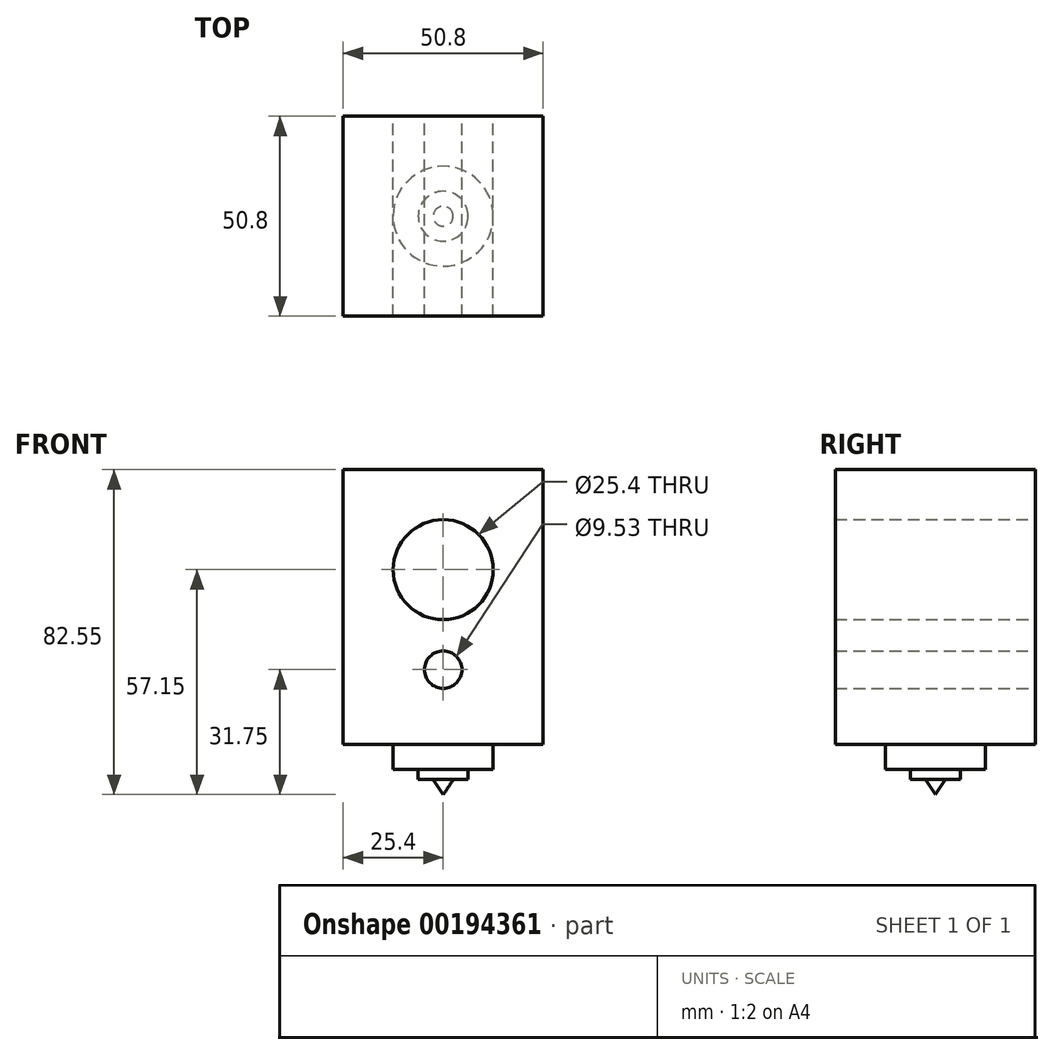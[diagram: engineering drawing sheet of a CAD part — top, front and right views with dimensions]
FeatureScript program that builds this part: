
annotation { "Feature Type Name" : "Feature", "Feature Type Description" : "" }
export const myFeature = defineFeature(function(context is Context, id is Id, definition is map)
    precondition{}
    {
        {
            var Q0;
            Q0=qCreatedBy(makeId("Front.planeOp"),FACE);
            var sketch = newSketch(context, id + "F0", { "sketchPlane" : qUnion([Q0])});
            skCircle(sketch, "E0", {"center": v(0, 0) * mm, "radius": 12.7 * mm});
            skCircle(sketch, "E1", {"center": v(0, -25.4) * mm, "radius": 4.76 * mm});
            skLineSegment(sketch, "E2.bottom", {"start": v(-25.4, -44.45) * mm, "end": v(25.4, -44.45) * mm});
            skLineSegment(sketch, "E2.top", {"start": v(-25.4, 25.4) * mm, "end": v(25.4, 25.4) * mm});
            skLineSegment(sketch, "E2.left", {"start": v(-25.4, -44.45) * mm, "end": v(-25.4, 25.4) * mm});
            skLineSegment(sketch, "E2.right", {"start": v(25.4, -44.45) * mm, "end": v(25.4, 25.4) * mm});
            skLineSegment(sketch, "E3", {"start": v(-12.7, -44.45) * mm, "end": v(-12.7, -50.8) * mm});
            skLineSegment(sketch, "E4", {"start": v(-12.7, -50.8) * mm, "end": v(12.7, -50.8) * mm});
            skLineSegment(sketch, "E5", {"start": v(12.7, -50.8) * mm, "end": v(12.7, -44.45) * mm});
            skLineSegment(sketch, "E6", {"start": v(-7.62, -50.8) * mm, "end": v(-7.62, -53.34) * mm});
            skLineSegment(sketch, "E7", {"start": v(-7.62, -53.34) * mm, "end": v(6.35, -53.34) * mm});
            skLineSegment(sketch, "E8", {"start": v(6.35, -53.34) * mm, "end": v(6.35, -50.8) * mm});
            skLineSegment(sketch, "E9", {"start": v(0, -53.34) * mm, "end": v(0, -57.15) * mm});
            skPoint(sketch, "E9.startSnap0", {"position": v(-0.63, -53.34) * mm});
            skLineSegment(sketch, "E10", {"start": v(0, -57.15) * mm, "end": v(2.54, -53.34) * mm});
            skLineSegment(sketch, "E11", {"start": v(0, -57.15) * mm, "end": v(-2.54, -53.34) * mm});
            skLineSegment(sketch, "E12", {"start": v(0, -25.4) * mm, "end": v(0, -57.15) * mm});
            skLineSegment(sketch, "E13", {"start": v(-2.54, -53.34) * mm, "end": v(0, -53.34) * mm});
            skLineSegment(sketch, "E14", {"start": v(2.54, -53.34) * mm, "end": v(0, -53.34) * mm});
            skSolve(sketch);
        }
        {
            var Q0;
            Q0=makeQuery(id+"F0.imprint","IMPRINT",FACE,{"disambiguationData":[TD([[makeQuery(id+"F0.imprint","IMPRINT",EDGE,{"derivedFrom":sQuery(id+"F0.wireOp",EDGE,"E0")}),-1.0]])]});
            extrude(context, id + "F1", {"entities" : qUnion([Q0]), "endBound" : BoundingType.SYMMETRIC, "depth" : 50.8 * mm});
        }
        {
            var Q0;
            {var subQ0=sQuery(id+"F0.wireOp",EDGE,"E5");Q0=makeQuery(id+"F0.imprint","IMPRINT",FACE,{"disambiguationData":[TD([[makeQuery(id+"F0.imprint","IMPRINT",EDGE,{"derivedFrom":subQ0}),1.0]])]});}
            var Q1;
            {var subQ4=sQuery(id+"F0.wireOp",EDGE,"E8");Q1=makeQuery(id+"F0.imprint","IMPRINT",FACE,{"disambiguationData":[TD([[makeQuery(id+"F0.imprint","IMPRINT",EDGE,{"derivedFrom":subQ4}),1.0]])]});}
            var Q2;
            {var subQ0=sQuery(id+"F0.wireOp",EDGE,"E10");Q2=makeQuery(id+"F0.imprint","IMPRINT",FACE,{"disambiguationData":[TD([[makeQuery(id+"F0.imprint","IMPRINT",EDGE,{"derivedFrom":subQ0}),1.0]])]});}
            var Q3;
            Q3=sQuery(id+"F0.wireOp",EDGE,"E12");
            revolve(context, id + "F2", {"operationType" : NewBodyOperationType.ADD, "entities" : qUnion([Q0, Q1, Q2]), "axis" : qUnion([Q3]), "revolveType" : RevolveType.FULL});
        }
    });
